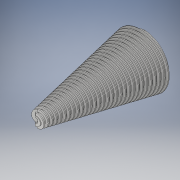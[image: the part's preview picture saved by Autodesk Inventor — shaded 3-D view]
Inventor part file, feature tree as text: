
AUTODESK INVENTOR PART (.ipt)
format: ipt  version: 2018 (Build 220112000, 112)  size: 1,205,248 bytes
history: native  units: in
note: dims shown in document units (in); Inventor stores cm internally (conversion verified against a paired STEP export)
features: sketch x8, extrude x3, helix x2, plane x1, loft x1, hole x1, other x1, projected_geometry x1
ambient origin geometry x8: Origin, YZ Plane, XZ Plane, XY Plane, X Axis, Y Axis, Z Axis, Center Point
bodies: Solid1 (feature_tree)
feature tree (18):
  sketch  "Sketch1"  dims[d0=2.0in d2=3.9in]
  plane  "Work Plane1"
  loft  "Loft1"
  hole  "Hole1"  [1 undecoded]
  other  "Work Axis2"
  sketch  "Sketch6"  dims[d83=1.0in d84=1.0in d11=0.185in d12=0.75in d13=0.375in d14=0.25in d15=0.5635in d16=1.0in d17=0.8108in d41=0.1in]
  helix  "Coil3"  [1 undecoded]
  helix  "Coil4"  [1 undecoded]
  sketch  "Sketch8"  dims[d42=0.1in d43=0.02in]
  sketch  "Sketch9"  dims[d44=0.13in d45=1.0in d46=11.811in d47=-0.0739in d48=90.0deg d49=90.0deg d50=0.0in d51=0.0in]
  extrude  "Extrusion2"  Depth=0.02in
  extrude  "Extrusion3"  Depth=3.775in
  extrude  "Extrusion4"  Depth=0.02in
  sketch  "Sketch2"  dims[d3=0.5in d5=0.0in d6=90.0deg d7=0.0in d8=90.0deg]
  projected_geometry  "Projected Loop1"
  sketch  "Sketch10"  dims[d52=0.13in d53=1.0in d54=11.811in d55=0.0756in d56=90.0deg d57=90.0deg d58=0.0in d59=0.0in d60=3.775in]
  sketch  "Sketch11"  dims[d61=0.02in d62=0.125in]
  sketch  "Sketch12"  dims[d65=0.0in d66=0.5in d69=0.0in d70=0.125in d73=0.02in d74=1.0in d75=0.0in d76=0.02in d77=0.125in d78=1.5in d79=3.0in d80=0.0in d81=0.02in d82=0.0in]
note: 3 required parameter values undecoded (feature->parameter linkage not recoverable at this tier; creation-order binding heuristic only, values carry confidence <= 0.55)
